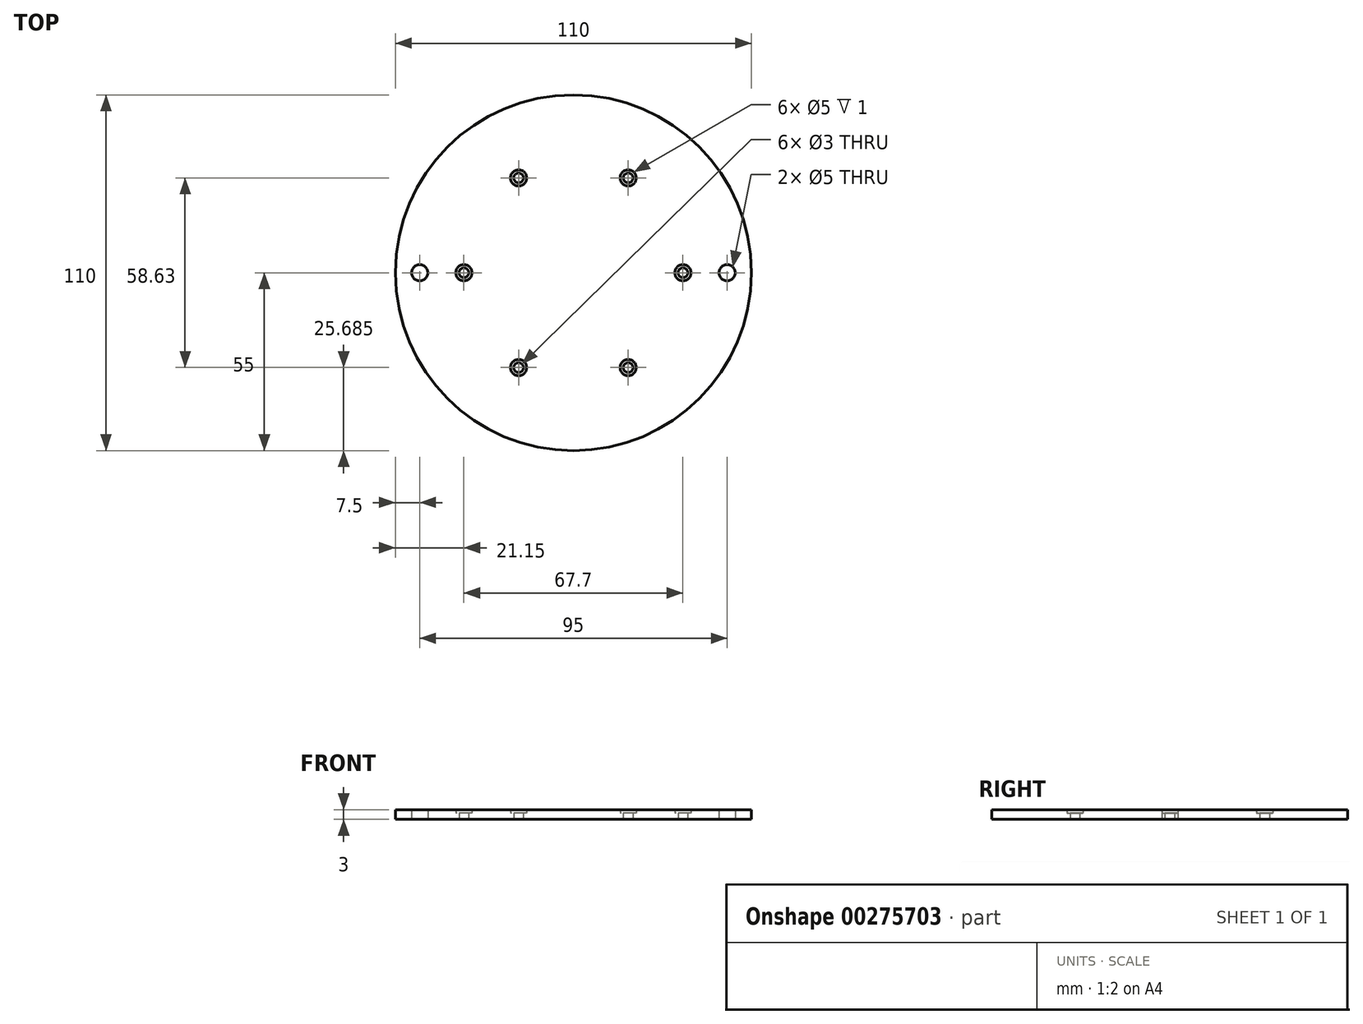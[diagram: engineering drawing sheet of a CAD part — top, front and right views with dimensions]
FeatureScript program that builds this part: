
annotation { "Feature Type Name" : "Feature", "Feature Type Description" : "" }
export const myFeature = defineFeature(function(context is Context, id is Id, definition is map)
    precondition{}
    {
        {
            var Q0;
            Q0=qCreatedBy(makeId("Top.planeOp"),FACE);
            var sketch = newSketch(context, id + "F0", { "sketchPlane" : qUnion([Q0])});
            skCircle(sketch, "E0", {"center": v(0, 0) * mm, "radius": 40 * mm});
            skCircle(sketch, "E1", {"center": v(0, 0) * mm, "radius": 55 * mm});
            skPoint(sketch, "E2", {"position": v(47.5, 0) * mm});
            skLineSegment(sketch, "E3", {"start": v(40, 0) * mm, "end": v(47.5, 0) * mm});
            skLineSegment(sketch, "E4", {"start": v(47.5, 0) * mm, "end": v(55, 0) * mm});
            skCircle(sketch, "E5", {"center": v(47.5, 0) * mm, "radius": 2.5 * mm});
            skCircle(sketch, "E6.MirrorC", {"center": v(-47.5, 0) * mm, "radius": 2.5 * mm});
            skCircle(sketch, "E7", {"center": v(0, 0) * mm, "radius": 33.85 * mm});
            skCircle(sketch, "E8", {"center": v(33.85, 0) * mm, "radius": 1.5 * mm});
            skCircle(sketch, "E9", {"center": v(33.85, 0) * mm, "radius": 2.5 * mm});
            skCircle(sketch, "E10.1.0", {"center": v(16.93, -29.31) * mm, "radius": 2.5 * mm});
            skCircle(sketch, "E10.1.1", {"center": v(16.93, -29.31) * mm, "radius": 1.5 * mm});
            skCircle(sketch, "E10.2.0", {"center": v(-16.93, -29.31) * mm, "radius": 2.5 * mm});
            skCircle(sketch, "E10.2.1", {"center": v(-16.93, -29.31) * mm, "radius": 1.5 * mm});
            skCircle(sketch, "E10.3.0", {"center": v(-33.85, 0) * mm, "radius": 2.5 * mm});
            skCircle(sketch, "E10.3.1", {"center": v(-33.85, 0) * mm, "radius": 1.5 * mm});
            skCircle(sketch, "E10.4.0", {"center": v(-16.92, 29.31) * mm, "radius": 2.5 * mm});
            skCircle(sketch, "E10.4.1", {"center": v(-16.92, 29.31) * mm, "radius": 1.5 * mm});
            skCircle(sketch, "E10.5.0", {"center": v(16.93, 29.31) * mm, "radius": 2.5 * mm});
            skCircle(sketch, "E10.5.1", {"center": v(16.93, 29.31) * mm, "radius": 1.5 * mm});
            skLineSegment(sketch, "E10.anchor1", {"start": v(0, 0) * mm, "end": v(33.85, 0) * mm, "construction": true});
            skLineSegment(sketch, "E10.anchor2", {"start": v(0, 0) * mm, "end": v(16.93, 29.31) * mm, "construction": true});
            skSolve(sketch);
        }
        {
            var Q0;
            {var subQ1=sQuery(id+"F0.wireOp",EDGE,"E7");var subQ7=sQuery(id+"F0.wireOp",EDGE,"E9");var subQ9=makeQuery(id+"F0.imprint","INTERSECT",VERTEX,{"disambiguationData":[OD(0.0)],"derivedFrom":[subQ1,subQ7]});Q0=makeQuery(id+"F0.imprint","IMPRINT",FACE,{"disambiguationData":[TD([[makeQuery(id+"F0.imprint","IMPRINT",EDGE,{"disambiguationData":[TD([[subQ9,-1.0]])],"derivedFrom":subQ1}),1.0]])]});}
            var Q1;
            Q1=makeQuery(id+"F0.imprint","IMPRINT",FACE,{"disambiguationData":[TD([[makeQuery(id+"F0.imprint","IMPRINT",EDGE,{"derivedFrom":sQuery(id+"F0.wireOp",EDGE,"E0")}),1.0]])]});
            var Q2;
            Q2=makeQuery(id+"F0.imprint","IMPRINT",FACE,{"disambiguationData":[TD([[makeQuery(id+"F0.imprint","IMPRINT",EDGE,{"derivedFrom":sQuery(id+"F0.wireOp",EDGE,"E0")}),-1.0]])]});
            extrude(context, id + "F1", {"entities" : qUnion([Q0, Q1, Q2]), "depth" : 3 * mm});
        }
        {
            var Q0;
            {var subQ0=sQuery(id+"F0.wireOp",EDGE,"E10.4.0");var subQ1=sQuery(id+"F0.wireOp",EDGE,"E7");var subQ2=makeQuery(id+"F0.imprint","INTERSECT",VERTEX,{"disambiguationData":[OD(0.0)],"derivedFrom":[subQ1,subQ0]});Q0=makeQuery(id+"F0.imprint","IMPRINT",FACE,{"disambiguationData":[TD([[makeQuery(id+"F0.imprint","IMPRINT",EDGE,{"disambiguationData":[TD([[subQ2,-1.0]])],"derivedFrom":subQ1}),1.0]])]});}
            var Q1;
            {var subQ0=sQuery(id+"F0.wireOp",EDGE,"E10.4.0");var subQ1=sQuery(id+"F0.wireOp",EDGE,"E7");var subQ2=makeQuery(id+"F0.imprint","INTERSECT",VERTEX,{"disambiguationData":[OD(0.0)],"derivedFrom":[subQ1,subQ0]});Q1=makeQuery(id+"F0.imprint","IMPRINT",FACE,{"disambiguationData":[TD([[makeQuery(id+"F0.imprint","IMPRINT",EDGE,{"disambiguationData":[TD([[subQ2,-1.0]])],"derivedFrom":subQ1}),-1.0]])]});}
            var Q2;
            {var subQ0=sQuery(id+"F0.wireOp",EDGE,"E10.3.0");var subQ1=sQuery(id+"F0.wireOp",EDGE,"E7");var subQ2=makeQuery(id+"F0.imprint","INTERSECT",VERTEX,{"disambiguationData":[OD(0.0)],"derivedFrom":[subQ1,subQ0]});Q2=makeQuery(id+"F0.imprint","IMPRINT",FACE,{"disambiguationData":[TD([[makeQuery(id+"F0.imprint","IMPRINT",EDGE,{"disambiguationData":[TD([[subQ2,-1.0]])],"derivedFrom":subQ1}),1.0]])]});}
            var Q3;
            {var subQ0=sQuery(id+"F0.wireOp",EDGE,"E10.3.0");var subQ1=sQuery(id+"F0.wireOp",EDGE,"E7");var subQ2=makeQuery(id+"F0.imprint","INTERSECT",VERTEX,{"disambiguationData":[OD(0.0)],"derivedFrom":[subQ1,subQ0]});Q3=makeQuery(id+"F0.imprint","IMPRINT",FACE,{"disambiguationData":[TD([[makeQuery(id+"F0.imprint","IMPRINT",EDGE,{"disambiguationData":[TD([[subQ2,-1.0]])],"derivedFrom":subQ1}),-1.0]])]});}
            var Q4;
            {var subQ0=sQuery(id+"F0.wireOp",EDGE,"E10.2.0");var subQ1=sQuery(id+"F0.wireOp",EDGE,"E7");var subQ2=makeQuery(id+"F0.imprint","INTERSECT",VERTEX,{"disambiguationData":[OD(0.0)],"derivedFrom":[subQ1,subQ0]});Q4=makeQuery(id+"F0.imprint","IMPRINT",FACE,{"disambiguationData":[TD([[makeQuery(id+"F0.imprint","IMPRINT",EDGE,{"disambiguationData":[TD([[subQ2,-1.0]])],"derivedFrom":subQ1}),1.0]])]});}
            var Q5;
            {var subQ0=sQuery(id+"F0.wireOp",EDGE,"E10.2.0");var subQ1=sQuery(id+"F0.wireOp",EDGE,"E7");var subQ2=makeQuery(id+"F0.imprint","INTERSECT",VERTEX,{"disambiguationData":[OD(0.0)],"derivedFrom":[subQ1,subQ0]});Q5=makeQuery(id+"F0.imprint","IMPRINT",FACE,{"disambiguationData":[TD([[makeQuery(id+"F0.imprint","IMPRINT",EDGE,{"disambiguationData":[TD([[subQ2,-1.0]])],"derivedFrom":subQ1}),-1.0]])]});}
            var Q6;
            {var subQ0=sQuery(id+"F0.wireOp",EDGE,"E10.1.0");var subQ1=sQuery(id+"F0.wireOp",EDGE,"E7");var subQ2=makeQuery(id+"F0.imprint","INTERSECT",VERTEX,{"disambiguationData":[OD(0.0)],"derivedFrom":[subQ1,subQ0]});Q6=makeQuery(id+"F0.imprint","IMPRINT",FACE,{"disambiguationData":[TD([[makeQuery(id+"F0.imprint","IMPRINT",EDGE,{"disambiguationData":[TD([[subQ2,-1.0]])],"derivedFrom":subQ1}),1.0]])]});}
            var Q7;
            {var subQ0=sQuery(id+"F0.wireOp",EDGE,"E10.1.0");var subQ1=sQuery(id+"F0.wireOp",EDGE,"E7");var subQ2=makeQuery(id+"F0.imprint","INTERSECT",VERTEX,{"disambiguationData":[OD(0.0)],"derivedFrom":[subQ1,subQ0]});Q7=makeQuery(id+"F0.imprint","IMPRINT",FACE,{"disambiguationData":[TD([[makeQuery(id+"F0.imprint","IMPRINT",EDGE,{"disambiguationData":[TD([[subQ2,-1.0]])],"derivedFrom":subQ1}),-1.0]])]});}
            var Q8;
            {var subQ0=sQuery(id+"F0.wireOp",EDGE,"E9");var subQ1=sQuery(id+"F0.wireOp",EDGE,"E7");var subQ2=makeQuery(id+"F0.imprint","INTERSECT",VERTEX,{"disambiguationData":[OD(0.0)],"derivedFrom":[subQ1,subQ0]});Q8=makeQuery(id+"F0.imprint","IMPRINT",FACE,{"disambiguationData":[TD([[makeQuery(id+"F0.imprint","IMPRINT",EDGE,{"disambiguationData":[TD([[subQ2,1.0]])],"derivedFrom":subQ1}),-1.0]])]});}
            var Q9;
            {var subQ0=sQuery(id+"F0.wireOp",EDGE,"E9");var subQ1=sQuery(id+"F0.wireOp",EDGE,"E7");var subQ2=makeQuery(id+"F0.imprint","INTERSECT",VERTEX,{"disambiguationData":[OD(0.0)],"derivedFrom":[subQ1,subQ0]});Q9=makeQuery(id+"F0.imprint","IMPRINT",FACE,{"disambiguationData":[TD([[makeQuery(id+"F0.imprint","IMPRINT",EDGE,{"disambiguationData":[TD([[subQ2,1.0]])],"derivedFrom":subQ1}),1.0]])]});}
            var Q10;
            {var subQ0=sQuery(id+"F0.wireOp",EDGE,"E10.5.0");var subQ1=sQuery(id+"F0.wireOp",EDGE,"E7");var subQ2=makeQuery(id+"F0.imprint","INTERSECT",VERTEX,{"disambiguationData":[OD(0.0)],"derivedFrom":[subQ1,subQ0]});Q10=makeQuery(id+"F0.imprint","IMPRINT",FACE,{"disambiguationData":[TD([[makeQuery(id+"F0.imprint","IMPRINT",EDGE,{"disambiguationData":[TD([[subQ2,-1.0]])],"derivedFrom":subQ1}),-1.0]])]});}
            var Q11;
            {var subQ0=sQuery(id+"F0.wireOp",EDGE,"E10.5.0");var subQ1=sQuery(id+"F0.wireOp",EDGE,"E7");var subQ2=makeQuery(id+"F0.imprint","INTERSECT",VERTEX,{"disambiguationData":[OD(0.0)],"derivedFrom":[subQ1,subQ0]});Q11=makeQuery(id+"F0.imprint","IMPRINT",FACE,{"disambiguationData":[TD([[makeQuery(id+"F0.imprint","IMPRINT",EDGE,{"disambiguationData":[TD([[subQ2,-1.0]])],"derivedFrom":subQ1}),1.0]])]});}
            extrude(context, id + "F2", {"entities" : qUnion([Q0, Q1, Q2, Q3, Q4, Q5, Q6, Q7, Q8, Q9, Q10, Q11]), "operationType" : NewBodyOperationType.ADD, "depth" : 2 * mm});
        }
    });
